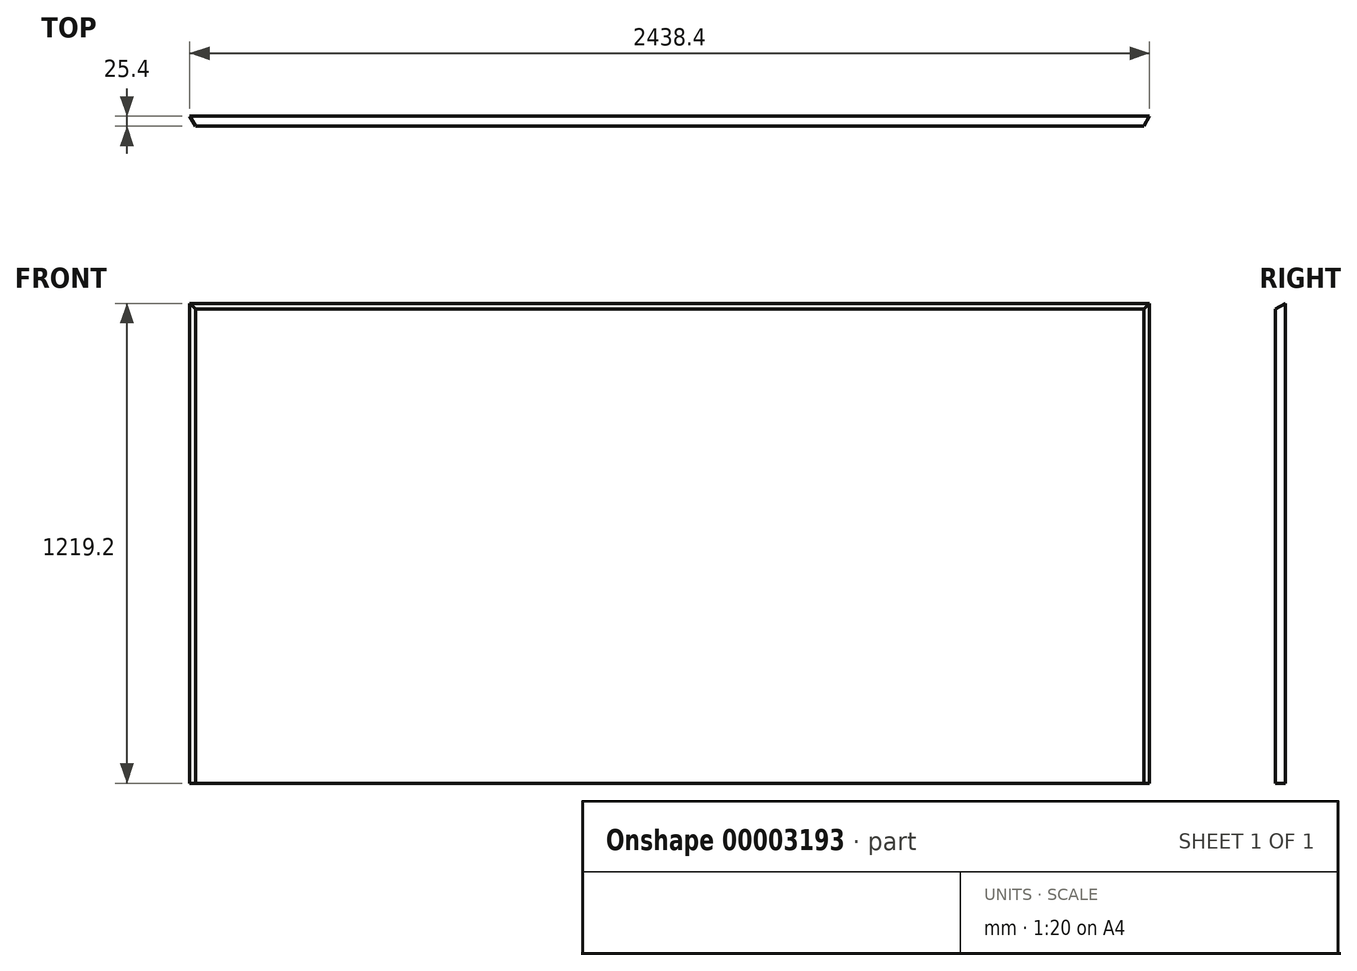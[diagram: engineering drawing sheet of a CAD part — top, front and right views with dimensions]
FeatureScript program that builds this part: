
annotation { "Feature Type Name" : "Feature", "Feature Type Description" : "" }
export const myFeature = defineFeature(function(context is Context, id is Id, definition is map)
    precondition{}
    {
        {
            var Q0;
            Q0=qCreatedBy(makeId("Front.planeOp"),FACE);
            var sketch = newSketch(context, id + "F0", { "sketchPlane" : qUnion([Q0])});
            skLineSegment(sketch, "E0.bottom", {"start": v(-1220.08, 50.95) * mm, "end": v(1218.32, 50.95) * mm});
            skLineSegment(sketch, "E0.top", {"start": v(-1220.08, -1168.25) * mm, "end": v(1218.32, -1168.25) * mm});
            skLineSegment(sketch, "E0.left", {"start": v(-1220.08, 50.95) * mm, "end": v(-1220.08, -1168.25) * mm});
            skLineSegment(sketch, "E0.right", {"start": v(1218.32, 50.95) * mm, "end": v(1218.32, -1168.25) * mm});
            skSolve(sketch);
        }
        {
            var Q0;
            Q0=makeQuery(id+"F0.imprint","IMPRINT",FACE,{"disambiguationData":[TD([[makeQuery(id+"F0.imprint","IMPRINT",EDGE,{"derivedFrom":sQuery(id+"F0.wireOp",EDGE,"E0.bottom")}),-1.0]])]});
            extrude(context, id + "F1", {"entities" : qUnion([Q0]), "depth" : 25.4 * mm});
        }
        {
            var Q0;
            Q0=makeQuery(id+"F1.opExtrude","CAP_EDGE",EDGE,{"disambiguationData":[OSD([sQuery(id+"F0.wireOp",EDGE,"E0.right")])],"isStart":false});
            chamfer(context, id + "F2", {"entities" : qUnion([Q0]), "chamferType" : ChamferType.OFFSET_ANGLE, "width" : 25.4 * mm, "oppositeDirection" : false, "angle" : 30 * degree, "tangentPropagation" : true});
        }
        {
            var Q0;
            Q0=makeQuery(id+"F1.opExtrude","CAP_EDGE",EDGE,{"disambiguationData":[OSD([sQuery(id+"F0.wireOp",EDGE,"E0.left")])],"isStart":false});
            chamfer(context, id + "F3", {"entities" : qUnion([Q0]), "chamferType" : ChamferType.OFFSET_ANGLE, "width" : 25.4 * mm, "oppositeDirection" : true, "angle" : 30 * degree, "tangentPropagation" : true});
        }
        {
            var Q0;
            Q0=makeQuery(id+"F1.opExtrude","CAP_EDGE",EDGE,{"disambiguationData":[OSD([sQuery(id+"F0.wireOp",EDGE,"E0.bottom")])],"isStart":false});
            chamfer(context, id + "F4", {"entities" : qUnion([Q0]), "chamferType" : ChamferType.OFFSET_ANGLE, "width" : 25.4 * mm, "oppositeDirection" : false, "angle" : 30 * degree, "tangentPropagation" : true});
        }
    });
